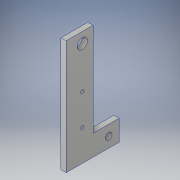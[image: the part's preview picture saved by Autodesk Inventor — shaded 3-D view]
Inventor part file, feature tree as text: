
AUTODESK INVENTOR PART (.ipt)
format: ipt  version: 2019 (Build 230136000, 136)  size: 133,120 bytes
history: native  units: in
note: dims shown in document units (in); Inventor stores cm internally (conversion verified against a paired STEP export)
features: sketch x3, extrude x2, hole x1, projected_geometry x1
ambient origin geometry x8: Origin, YZ Plane, XZ Plane, XY Plane, X Axis, Y Axis, Z Axis, Center Point
bodies: Solid1 (feature_tree)
feature tree (7):
  extrude  "Extrusion1"  Depth=5.5in
  hole  "Hole1"  [1 undecoded]
  extrude  "Extrusion2"  Depth=0.25in
  sketch  "Sketch1"  dims[d0=5.5in d2=0.5in]
  sketch  "Sketch2"  dims[d3=0.32in d5=4.5in]
  sketch  "Sketch3"  dims[d6=0.5in d7=0.5in d8=0.522in d9=0.5in d10=0.25in d11=0.0in d12=3.0in d13=1.5in d14=1.044in d15=0.522in d16=0.522in d17=0.15in d18=0.75in d19=0.375in d20=0.25in d21=0.5635in d22=1.0in d23=0.8108in d24=1.044in d26=1.272in d27=0.25in d28=0.0in]
  projected_geometry  "Projected Loop1"
note: 1 required parameter value undecoded (feature->parameter linkage not recoverable at this tier; creation-order binding heuristic only, values carry confidence <= 0.55)
